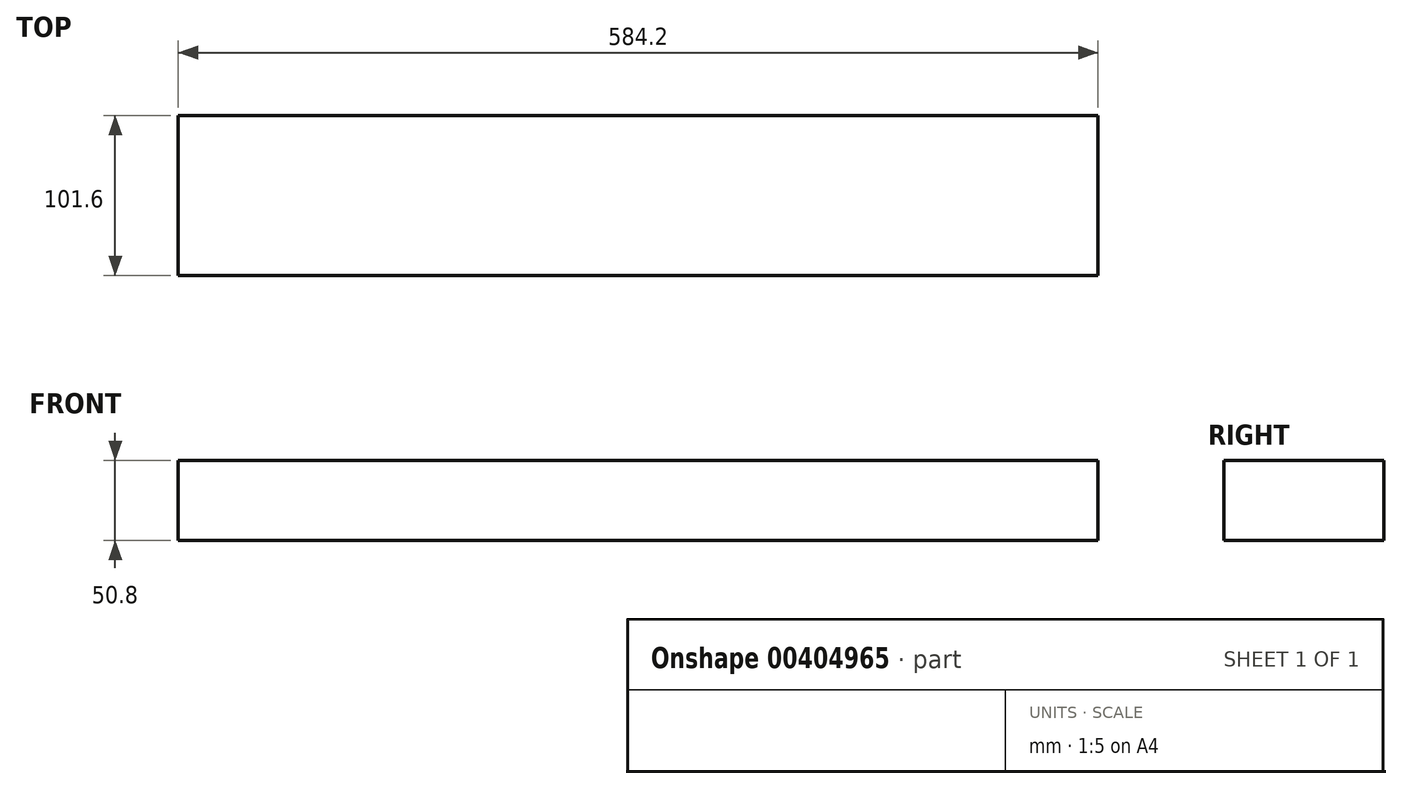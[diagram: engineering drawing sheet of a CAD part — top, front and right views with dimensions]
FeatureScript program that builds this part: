
annotation { "Feature Type Name" : "Feature", "Feature Type Description" : "" }
export const myFeature = defineFeature(function(context is Context, id is Id, definition is map)
    precondition{}
    {
        {
            var Q0;
            Q0=qCreatedBy(makeId("Right.planeOp"),FACE);
            var sketch = newSketch(context, id + "F0", { "sketchPlane" : qUnion([Q0])});
            skLineSegment(sketch, "E0.bottom", {"start": v(0, 0) * mm, "end": v(101.6, 0) * mm});
            skLineSegment(sketch, "E0.top", {"start": v(0, 50.8) * mm, "end": v(101.6, 50.8) * mm});
            skLineSegment(sketch, "E0.left", {"start": v(0, 0) * mm, "end": v(0, 50.8) * mm});
            skLineSegment(sketch, "E0.right", {"start": v(101.6, 0) * mm, "end": v(101.6, 50.8) * mm});
            skSolve(sketch);
        }
        {
            var Q0;
            Q0=qSketchRegion(id+"F0",true);
            extrude(context, id + "F1", {"entities" : qUnion([Q0]), "depth" : 584.2 * mm});
        }
    });
